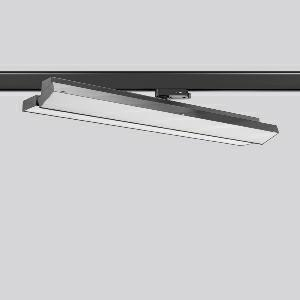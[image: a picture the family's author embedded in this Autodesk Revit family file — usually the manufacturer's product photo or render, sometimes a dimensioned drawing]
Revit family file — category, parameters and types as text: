
# Revit family: tx-move_742164_003_3_76_c482
name_source: partatom
category: Lighting Fixtures
units: mm (PartAtom-declared; Revit-internal decimal feet)

## family parameters
Cut with Voids When Loaded = No
Host = Face
Light Source = No
Part Type = Normal
Room Calculation Point = No
Round Connector Dimension = Use Diameter
Shared = No

## types (1)
- MultiLumen 1 (1 x LED Modul 835, 2550 lm, 3500)
    Apparent Load = 41 VA
    CIE Flux Codes = 47 79 96 100 100
    Color Rendering = 80
    Color Temperature = 3500
    Default Elevation = 1800 mm
    Description = Series: TX-MOVE
Multifunctional surface-mounted spotlight for area lighting. Very flat design. Housing: sheet steel, powder-coated. Rotation range: 356°. Swivel range: 90°. Consistent alignment possible with visible tilt scale. High-efficiency LED units with flush-mounted opal diffuser made of non-yellowing PMMA. Symmetrical wide beam light emission. With adapter for RZB 3-circuit DALI tracks. Suitable for Track on ceiling. MultiLumen: Luminous flux adjustable in 3 steps. Factory setting is the highest luminous flux. Environmentally friendly and resource-saving due to replaceable and recyclable components. 
Colour: deep black, matt (RAL 9005)
Length: 570 mm
Width: 119 mm
Height: 88 mm
Lamp: LED
Socket: without socket
Colour temperature: 3500K
Colour rendering index (CRI): 80
System power: 41 W
Rated luminous flux: 5100 lm
Luminous efficiency: 124 lm/W
System power 2: 57 W
Rated luminous flux 2: 6950 lm
Luminous efficiency 2: 122 lm/W
System power 3: 73 W
Rated luminous flux 3: 8500 lm
Luminous efficiency 3: 116 lm/W
Control gear: Dimmable EVG, DALI
Protection class: I
Type of protection: IP 20
    Height = 75 mm
    Lamp = 1 x LED Modul 835
    Lamp Light Flux = 2550 lm
    Lamp count = 1
    Length = 569 mm
    Lifetime = 50000 h
    Luminous efficacy = 124 lm/W
    Manufacturer = RZB
    ModVariant = No
    Model = 742164.003.3.76
    Mounting Place = Ceiling
    Mounting Type = Rail mounted
    Number of Poles = 1
    OnlyDefault = Yes
    Power Factor = 1
    Product Name = TX-MOVE
    Product group = Track mounted projectors
    ProductGroupID = 301
    Protection Class = Protection class I
    Protection Degree = IP 20
    RLX_Detail_Level = 1
    RLX_Emergency_Light_Flux = 0 lm
    RLX_Emergency_Type = 0
    RLX_Emergency_Type_DB = No
    RlxData = <blob elided: 35885 chars, md5=6251c379>
    Socket = socket
    Standby Power = 0 W
    System Light Flux = 5100 lm
    System Power = 41 W
    Type Comments = MultiLumen 1
    Type Image = 742164.003.jpg
    URL = http://relux.com
    VarID = multilumen_1
    Voltage = 230 V
    Voltage Range = 220-240 V
    Weight = 0.00 kg
    Width = 119 mm

## geometry (parser evidence)
native form markers: Blend x4, Sweep x14
no freeform markers — native parametric forms only
